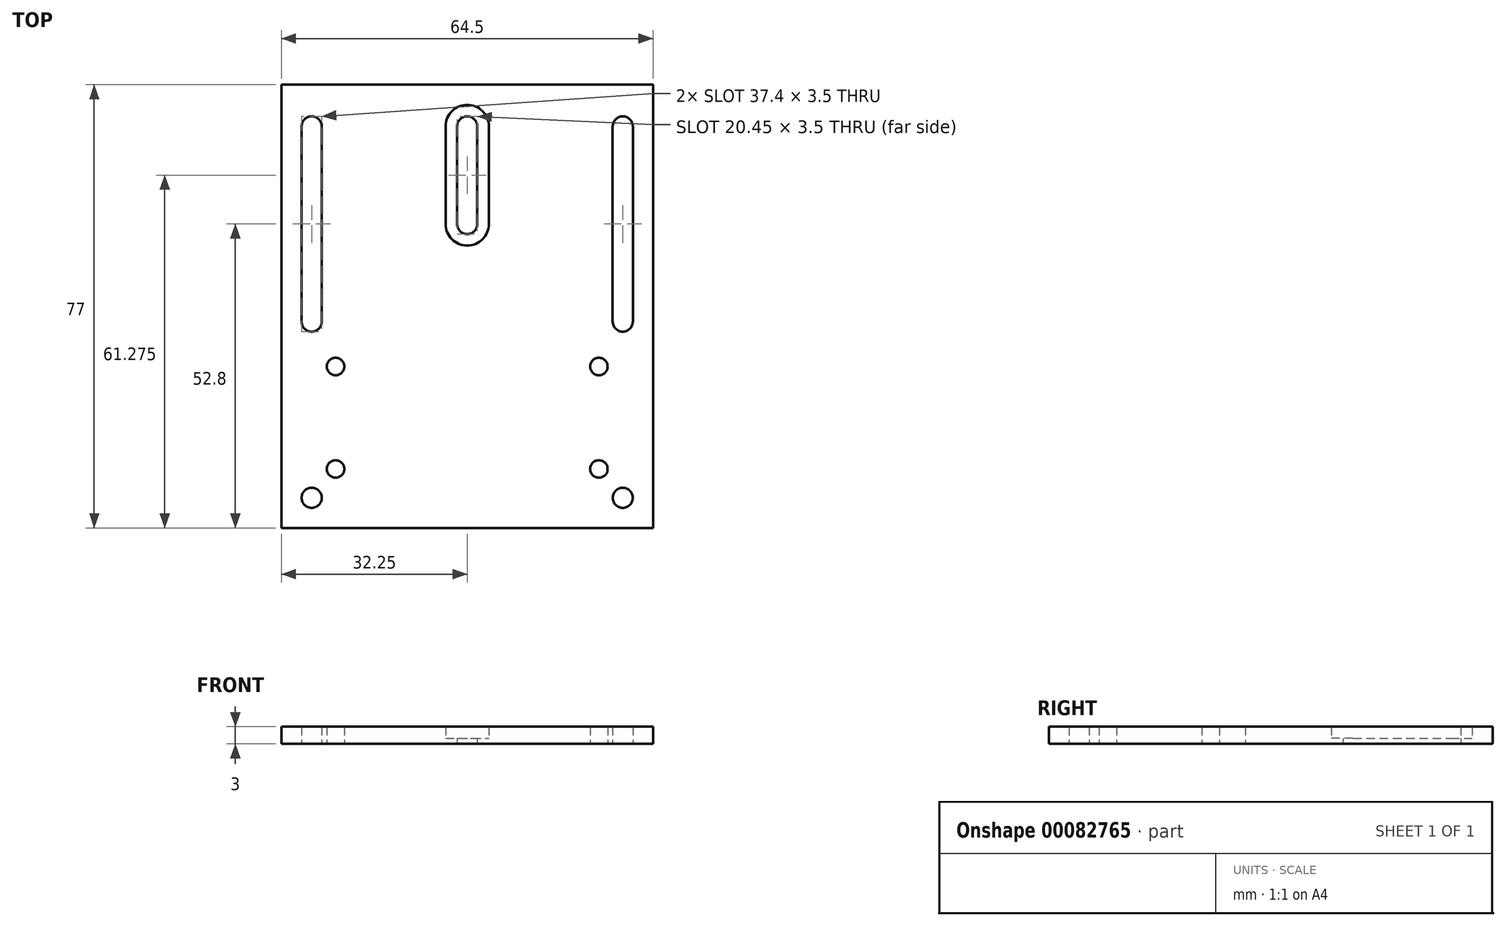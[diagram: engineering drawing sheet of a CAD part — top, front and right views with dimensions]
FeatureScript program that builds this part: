
annotation { "Feature Type Name" : "Feature", "Feature Type Description" : "" }
export const myFeature = defineFeature(function(context is Context, id is Id, definition is map)
    precondition{}
    {
        {
            var Q0;
            Q0=qCreatedBy(makeId("Top.planeOp"),FACE);
            var sketch = newSketch(context, id + "F0", { "sketchPlane" : qUnion([Q0])});
            skLineSegment(sketch, "E0", {"start": v(0, 0) * mm, "end": v(64.5, 0) * mm});
            skLineSegment(sketch, "E1", {"start": v(64.5, 0) * mm, "end": v(64.5, 77) * mm});
            skLineSegment(sketch, "E2", {"start": v(64.5, 77) * mm, "end": v(0, 77) * mm});
            skLineSegment(sketch, "E3", {"start": v(0, 77) * mm, "end": v(0, 0) * mm});
            skLineSegment(sketch, "E4", {"start": v(6.85, 30.6) * mm, "end": v(6.85, 7.7) * mm, "construction": true});
            skLineSegment(sketch, "E5", {"start": v(6.85, 7.7) * mm, "end": v(57.65, 7.7) * mm, "construction": true});
            skLineSegment(sketch, "E6", {"start": v(57.65, 7.7) * mm, "end": v(57.65, 30.6) * mm, "construction": true});
            skLineSegment(sketch, "E7", {"start": v(57.65, 30.6) * mm, "end": v(6.85, 30.6) * mm, "construction": true});
            skLineSegment(sketch, "E8", {"start": v(6.85, 19.15) * mm, "end": v(57.65, 19.15) * mm, "construction": true});
            skCircle(sketch, "E9", {"center": v(5.25, 5.25) * mm, "radius": 1.75 * mm});
            skPoint(sketch, "E10", {"position": v(32.25, 30.6) * mm});
            skLineSegment(sketch, "E11", {"start": v(32.25, 77) * mm, "end": v(32.25, 0) * mm, "construction": true});
            skLineSegment(sketch, "E12", {"start": v(0, 38.5) * mm, "end": v(64.5, 38.5) * mm, "construction": true});
            skCircle(sketch, "E13.MirrorC", {"center": v(59.25, 5.25) * mm, "radius": 1.75 * mm});
            skLineSegment(sketch, "E14", {"start": v(3.5, 35.85) * mm, "end": v(3.5, 69.75) * mm});
            skLineSegment(sketch, "E15", {"start": v(3.5, 69.75) * mm, "end": v(7, 69.75) * mm});
            skLineSegment(sketch, "E16", {"start": v(7, 69.75) * mm, "end": v(7, 35.85) * mm});
            skLineSegment(sketch, "E17", {"start": v(7, 35.85) * mm, "end": v(3.5, 35.85) * mm});
            skArc(sketch, "E18", {"start": v(3.5, 35.85) * mm, "mid": v(5.25, 34.1) * mm, "end": v(7, 35.85) * mm});
            skArc(sketch, "E19", {"start": v(7, 69.75) * mm, "mid": v(5.25, 71.5) * mm, "end": v(3.5, 69.75) * mm});
            skLineSegment(sketch, "E20.MirrorCS", {"start": v(61, 35.85) * mm, "end": v(61, 69.75) * mm});
            skLineSegment(sketch, "E21.MirrorCS", {"start": v(57.5, 69.75) * mm, "end": v(57.5, 35.85) * mm});
            skArc(sketch, "E22.MirrorCS", {"start": v(57.5, 69.75) * mm, "mid": v(59.25, 71.5) * mm, "end": v(61, 69.75) * mm});
            skArc(sketch, "E23.MirrorCS", {"start": v(61, 35.85) * mm, "mid": v(59.25, 34.1) * mm, "end": v(57.5, 35.85) * mm});
            skCircle(sketch, "E24", {"center": v(9.4, 10.25) * mm, "radius": 1.52 * mm});
            skCircle(sketch, "E25.MirrorC", {"center": v(9.4, 28.05) * mm, "radius": 1.52 * mm});
            skCircle(sketch, "E26", {"center": v(55.1, 10.25) * mm, "radius": 1.52 * mm});
            skCircle(sketch, "E27.MirrorC", {"center": v(55.1, 28.05) * mm, "radius": 1.52 * mm});
            skPoint(sketch, "E28", {"position": v(9.4, 19.15) * mm});
            skPoint(sketch, "E29", {"position": v(32.25, 10.25) * mm});
            skArc(sketch, "E30", {"start": v(34, 69.75) * mm, "mid": v(32.25, 71.5) * mm, "end": v(30.5, 69.75) * mm});
            skArc(sketch, "E31", {"start": v(30.5, 52.8) * mm, "mid": v(32.25, 51.05) * mm, "end": v(34, 52.8) * mm});
            skLineSegment(sketch, "E32", {"start": v(34, 52.8) * mm, "end": v(34, 69.75) * mm});
            skLineSegment(sketch, "E33", {"start": v(30.5, 52.8) * mm, "end": v(30.5, 69.75) * mm});
            skLineSegment(sketch, "E34", {"start": v(7, 52.8) * mm, "end": v(57.5, 52.8) * mm, "construction": true});
            skLineSegment(sketch, "E35.0", {"start": v(36, 52.8) * mm, "end": v(36, 69.75) * mm});
            skArc(sketch, "E35.1", {"start": v(28.5, 52.8) * mm, "mid": v(32.25, 49.05) * mm, "end": v(36, 52.8) * mm});
            skLineSegment(sketch, "E35.2", {"start": v(28.5, 52.8) * mm, "end": v(28.5, 69.75) * mm});
            skArc(sketch, "E35.3", {"start": v(36, 69.75) * mm, "mid": v(32.25, 73.5) * mm, "end": v(28.5, 69.75) * mm});
            skSolve(sketch);
        }
        {
            var Q0;
            Q0=makeQuery(id+"F0.imprint","IMPRINT",FACE,{"disambiguationData":[TD([[makeQuery(id+"F0.imprint","IMPRINT",EDGE,{"derivedFrom":sQuery(id+"F0.wireOp",EDGE,"E0")}),1.0]])]});
            extrude(context, id + "F1", {"entities" : qUnion([Q0]), "depth" : 3 * mm});
        }
        {
            var Q0;
            Q0=makeQuery(id+"F0.imprint","IMPRINT",FACE,{"disambiguationData":[TD([[makeQuery(id+"F0.imprint","IMPRINT",EDGE,{"derivedFrom":sQuery(id+"F0.wireOp",EDGE,"E30")}),-1.0]])]});
            extrude(context, id + "F2", {"entities" : qUnion([Q0]), "operationType" : NewBodyOperationType.ADD, "depth" : 1 * mm});
        }
    });
